# Revit family: NLRS_57_DUF_UN_round-end-cap_LT_velu
name_source: partatom
category: Duct Fittings
units: mm (PartAtom-declared; Revit-internal decimal feet)

## family parameters
Always vertical = Yes
Cut with Voids When Loaded = No
OmniClass Number = 23.75.70.14
OmniClass Title = Air Ductwork
Part Type = Cap
Round Connector Dimension = Use Diameter
Shared = No
Work Plane-Based = No

## types (1)
- SGN
    Assembly Code = 57.00
    Default Elevation = 0 mm  [stored 0 ft]
    Description = Rond deksel
    IfcDescription = Rond deksel
    IfcExportAs = IfcDuctFittingType
    IfcExportType = USERDEFINED
    Manufacturer = Velu Klimaattechnische groothandel
    Model = Velu rond deksel
    NLRS_C_bestemming = Ventilatiesystemen
    NLRS_C_content_datum_gewijzigd = 30-11-2023
    NLRS_C_content_provider = Velu Klimaattechnische groothandel
    NLRS_C_content_versie = 3.21.01
    NLRS_C_description = Rond deksel
    Type Image = <None>
    URL = https://webshop.velu.nl
    VELU_Article_Data = SGN
    VELU_Article_Data2 = VH

note: [stored X ft] marks values corroborated as IEEE doubles in the binary element streams (Revit-internal decimal feet)

## geometry (parser evidence)
native form markers: Sweep x8
no freeform markers — native parametric forms only
